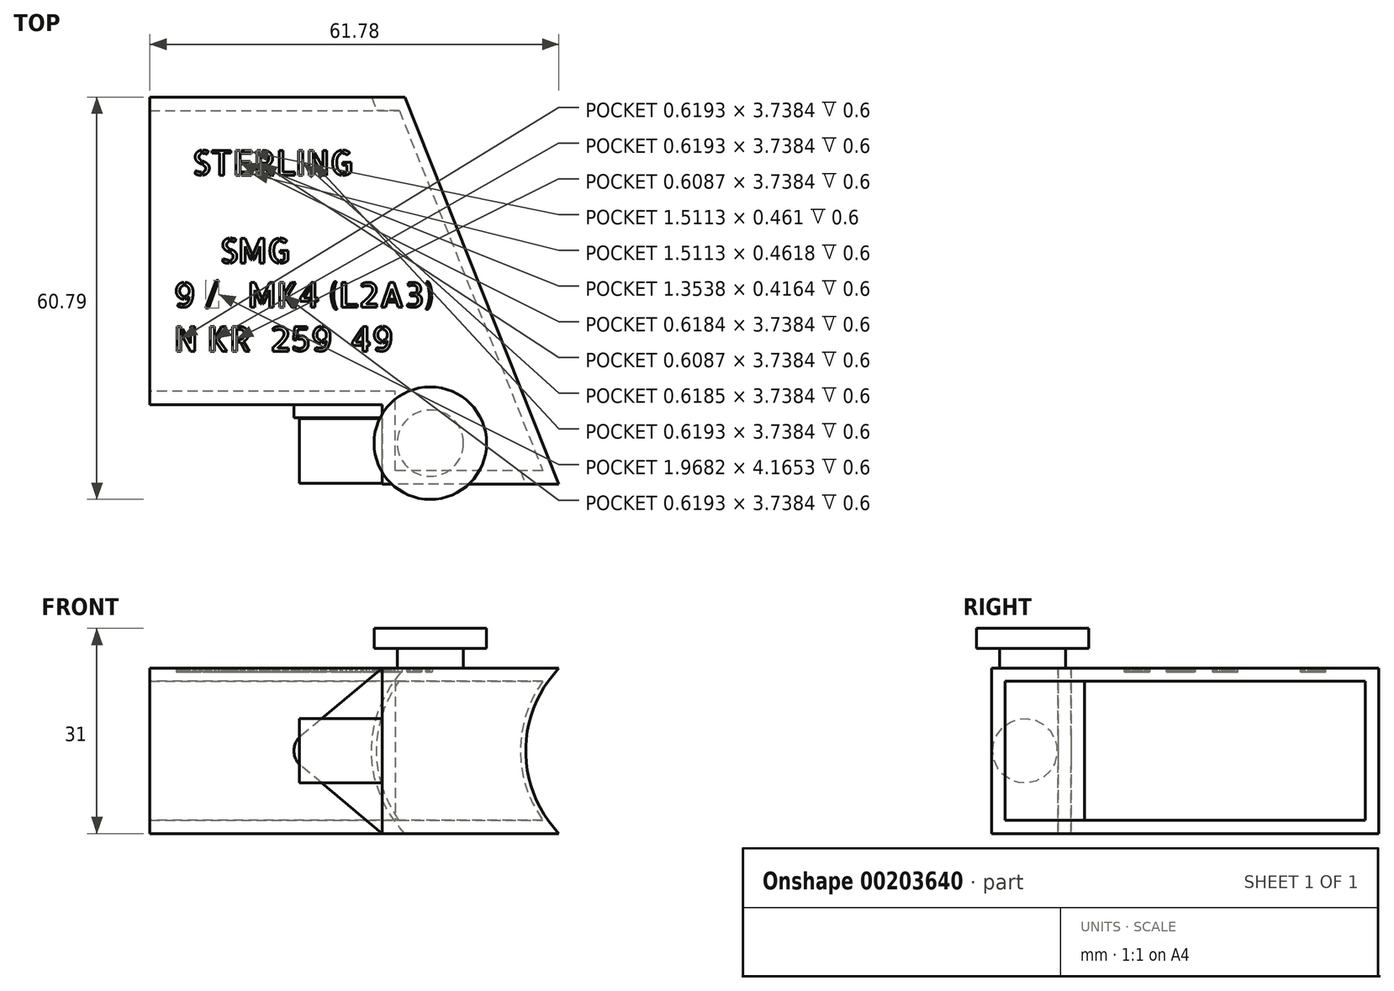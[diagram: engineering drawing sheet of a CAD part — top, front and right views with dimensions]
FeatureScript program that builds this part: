
annotation { "Feature Type Name" : "Feature", "Feature Type Description" : "" }
export const myFeature = defineFeature(function(context is Context, id is Id, definition is map)
    precondition{}
    {
        {
            var Q0;
            Q0=qCreatedBy(makeId("Top.planeOp"),FACE);
            var sketch = newSketch(context, id + "F0", { "sketchPlane" : qUnion([Q0])});
            skLineSegment(sketch, "E0", {"start": v(0, 0) * mm, "end": v(-52.95, 21.09) * mm});
            skLineSegment(sketch, "E1", {"start": v(-52.95, 21.09) * mm, "end": v(-35.77, 64.24) * mm});
            skLineSegment(sketch, "E2", {"start": v(-35.77, 64.24) * mm, "end": v(0, 50) * mm});
            skLineSegment(sketch, "E3", {"start": v(0, 50) * mm, "end": v(0, 0) * mm});
            skLineSegment(sketch, "E4", {"start": v(0, 0) * mm, "end": v(0, -12.92) * mm});
            skLineSegment(sketch, "E5", {"start": v(0, -12.92) * mm, "end": v(-24.8, -3.04) * mm});
            skLineSegment(sketch, "E6", {"start": v(-24.8, -3.04) * mm, "end": v(-20.37, 8.11) * mm});
            skSolve(sketch);
        }
        {
            var Q0;
            Q0 = qSketchRegion(id + "F0", true);
            extrude(context, id + "F1", {"entities" : qUnion([Q0]), "depth" : 25 * mm});
        }
        {
            var Q0;
            Q0=qCreatedBy(makeId("Front.planeOp"),FACE);
            var sketch = newSketch(context, id + "F2", { "sketchPlane" : qUnion([Q0])});
            skCircle(sketch, "E7", {"center": v(14.38, 12.5) * mm, "radius": 19.05 * mm});
            skSolve(sketch);
        }
        {
            var Q0;
            Q0 = qSketchRegion(id + "F2", true);
            extrude(context, id + "F3", {"entities" : qUnion([Q0]), "operationType" : NewBodyOperationType.REMOVE, "endBound" : BoundingType.THROUGH_ALL, "oppositeDirection" : true, "depth" : 25 * mm, "hasSecondDirection" : true, "secondDirectionBound" : SecondDirectionBoundingType.THROUGH_ALL, "secondDirectionOppositeDirection" : false, "secondDirectionDepth" : 25 * mm});
        }
        {
            var Q0;
            Q0=makeQuery(id+"F1.opExtrude","SWEPT_FACE",FACE,{"disambiguationData":[OSD([sQuery(id+"F0.wireOp",EDGE,"E1")])]});
            var Q1;
            Q1=makeQuery(id+"F3.boolean.opBoolean","COPY",FACE,{"derivedFrom":makeQuery(id+"F3.opExtrude","SWEPT_FACE",FACE,{"disambiguationData":[OSD([sQuery(id+"F2.wireOp",EDGE,"E7")])]})});
            shell(context, id + "F4", {"entities" : qUnion([Q0, Q1]), "thickness" : 2 * mm});
        }
        {
            var Q0;
            Q0=makeQuery(id+"F1.opExtrude","SWEPT_FACE",FACE,{"disambiguationData":[OSD([sQuery(id+"F0.wireOp",EDGE,"E0")])]});
            var sketch = newSketch(context, id + "F5", { "sketchPlane" : qUnion([Q0])});
            skLineSegment(sketch, "E8", {"start": v(-21.92, 0) * mm, "end": v(-34.16, 10.2) * mm});
            skPoint(sketch, "E8.endSnap0", {"position": v(-57, 12.5) * mm});
            skLineSegment(sketch, "E9", {"start": v(-34.16, 14.8) * mm, "end": v(-21.92, 25) * mm});
            skLineSegment(sketch, "E10", {"start": v(-21.92, 25) * mm, "end": v(-21.92, 0) * mm});
            skPoint(sketch, "E11.visualSharp", {"position": v(-36.92, 12.5) * mm});
            skArc(sketch, "E11.filletArc", {"start": v(-34.16, 14.8) * mm, "mid": v(-35.23, 12.5) * mm, "end": v(-34.16, 10.2) * mm});
            skSolve(sketch);
        }
        {
            var Q0;
            Q0 = qSketchRegion(id + "F5", true);
            extrude(context, id + "F6", {"entities" : qUnion([Q0]), "operationType" : NewBodyOperationType.ADD, "depth" : 2 * mm});
        }
        {
            var Q0;
            Q0=makeQuery(id+"F1.opExtrude","SWEPT_FACE",FACE,{"disambiguationData":[OSD([sQuery(id+"F0.wireOp",EDGE,"E6")])]});
            var sketch = newSketch(context, id + "F7", { "sketchPlane" : qUnion([Q0])});
            skCircle(sketch, "E12", {"center": v(7, 12.5) * mm, "radius": 4.87 * mm});
            skPoint(sketch, "E12.centerSnap1", {"position": v(7, 0) * mm});
            skSolve(sketch);
        }
        {
            var Q0;
            Q0 = qSketchRegion(id + "F7", true);
            extrude(context, id + "F8", {"entities" : qUnion([Q0]), "operationType" : NewBodyOperationType.ADD, "depth" : 12.5 * mm});
        }
        {
            var Q0;
            Q0=makeQuery(id+"F1.opExtrude","CAP_FACE",FACE,{"disambiguationData":[OSD([sQuery(id+"F0.wireOp",EDGE,"E0"),sQuery(id+"F0.wireOp",EDGE,"E1"),sQuery(id+"F0.wireOp",EDGE,"E2"),sQuery(id+"F0.wireOp",EDGE,"E3"),sQuery(id+"F0.wireOp",EDGE,"E4"),sQuery(id+"F0.wireOp",EDGE,"E5"),sQuery(id+"F0.wireOp",EDGE,"E6")])],"isStart":false});
            var sketch = newSketch(context, id + "F9", { "sketchPlane" : qUnion([Q0])});
            skCircle(sketch, "E13", {"center": v(-15.76, 0) * mm, "radius": 5 * mm});
            skSolve(sketch);
        }
        {
            var Q0;
            Q0 = qSketchRegion(id + "F9", true);
            extrude(context, id + "F10", {"entities" : qUnion([Q0]), "operationType" : NewBodyOperationType.ADD, "depth" : 3 * mm});
        }
        {
            var Q0;
            Q0=makeQuery(id+"F10.opExtrude","CAP_FACE",FACE,{"disambiguationData":[OSD([sQuery(id+"F9.wireOp",EDGE,"E13")])],"isStart":false});
            var sketch = newSketch(context, id + "F11", { "sketchPlane" : qUnion([Q0])});
            skCircle(sketch, "E14", {"center": v(-15.76, 0) * mm, "radius": 8.5 * mm});
            skSolve(sketch);
        }
        {
            var Q0;
            Q0 = qSketchRegion(id + "F11", true);
            extrude(context, id + "F12", {"entities" : qUnion([Q0]), "operationType" : NewBodyOperationType.ADD, "depth" : 3 * mm});
        }
        {
            var Q0;
            Q0=makeQuery(id+"F1.opExtrude","SWEPT_BODY",BODY,{"disambiguationData":[OSD([sQuery(id+"F0.wireOp",EDGE,"E0"),sQuery(id+"F0.wireOp",EDGE,"E1"),sQuery(id+"F0.wireOp",EDGE,"E2"),sQuery(id+"F0.wireOp",EDGE,"E3"),sQuery(id+"F0.wireOp",EDGE,"E4"),sQuery(id+"F0.wireOp",EDGE,"E5"),sQuery(id+"F0.wireOp",EDGE,"E6")])]});
            var Q1;
            Q1=makeQuery(id+"F1.opExtrude","SWEPT_EDGE",EDGE,{"disambiguationData":[OSD([sQuery(id+"F0.wireOp",EDGE,"E1"),sQuery(id+"F0.wireOp",EDGE,"E2")])]});
            transform(context, id + "F13", {"entities" : qUnion([Q0]), "transformType" : TransformType.ROTATION, "transformAxis" : qUnion([Q1]), "angle" : 21.72 * degree, "oppositeDirection" : true, "makeCopy" : false});
        }
        {
            var Q0;
            Q0=makeQuery(id+"F1.opExtrude","CAP_FACE",FACE,{"disambiguationData":[OSD([sQuery(id+"F0.wireOp",EDGE,"E0"),sQuery(id+"F0.wireOp",EDGE,"E1"),sQuery(id+"F0.wireOp",EDGE,"E2"),sQuery(id+"F0.wireOp",EDGE,"E3"),sQuery(id+"F0.wireOp",EDGE,"E4"),sQuery(id+"F0.wireOp",EDGE,"E5"),sQuery(id+"F0.wireOp",EDGE,"E6")])],"isStart":false});
            var sketch = newSketch(context, id + "F14", { "sketchPlane" : qUnion([Q0])});
            skText(sketch, "E15", { "text": "  STERLING\n\n     SMG\n9 /   MK4 (L2A3)\nN KR  259  49", "fontName": "AllertaStencil-Regular.ttf"});
            const initialGuessF14  = {"E15": [-0.03216, 0.05246, 1, 0, 0.00374]};
            skSetInitialGuess(sketch, initialGuessF14);
            skSolve(sketch);
        }
        {
            var Q0;
            Q0 = qSketchRegion(id + "F14", true);
            extrude(context, id + "F15", {"entities" : qUnion([Q0]), "operationType" : NewBodyOperationType.REMOVE, "oppositeDirection" : true, "depth" : .6 * mm});
        }
    });
